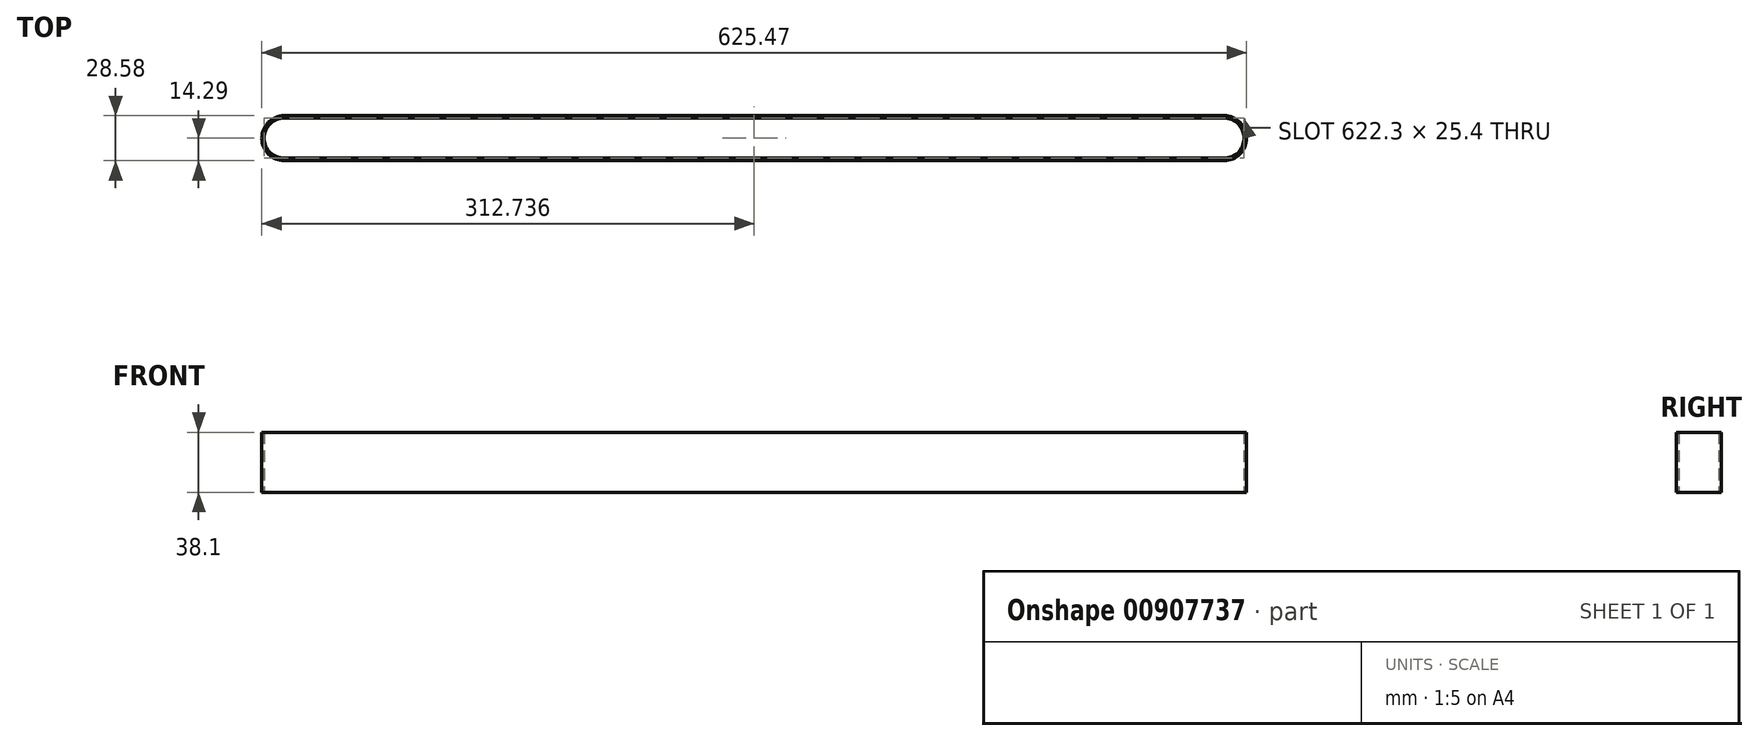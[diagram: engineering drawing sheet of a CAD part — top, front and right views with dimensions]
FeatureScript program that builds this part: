
annotation { "Feature Type Name" : "Feature", "Feature Type Description" : "" }
export const myFeature = defineFeature(function(context is Context, id is Id, definition is map)
    precondition{}
    {
        {
            var Q0;
            Q0=qCreatedBy(makeId("Top.planeOp"),FACE);
            var sketch = newSketch(context, id + "F0", { "sketchPlane" : qUnion([Q0])});
            skArc(sketch, "E0", {"start": v(-70.61, 14.29) * mm, "mid": v(-84.9, 0) * mm, "end": v(-70.61, -14.29) * mm});
            skArc(sketch, "E1", {"start": v(526.29, -14.29) * mm, "mid": v(540.57, 0) * mm, "end": v(526.29, 14.29) * mm});
            skLineSegment(sketch, "E2", {"start": v(-70.61, 14.29) * mm, "end": v(526.29, 14.29) * mm});
            skLineSegment(sketch, "E3", {"start": v(526.29, -14.29) * mm, "end": v(-70.61, -14.29) * mm});
            skArc(sketch, "E4", {"start": v(-70.61, 12.7) * mm, "mid": v(-83.31, 0) * mm, "end": v(-70.61, -12.7) * mm});
            skArc(sketch, "E5", {"start": v(526.29, -12.7) * mm, "mid": v(538.99, 0) * mm, "end": v(526.29, 12.7) * mm});
            skLineSegment(sketch, "E6", {"start": v(-70.61, 12.7) * mm, "end": v(526.29, 12.7) * mm});
            skLineSegment(sketch, "E7", {"start": v(526.29, -12.7) * mm, "end": v(-70.61, -12.7) * mm});
            skSolve(sketch);
        }
        {
            var Q0;
            Q0 = qSketchRegion(id + "F0", true);
            extrude(context, id + "F1", {"entities" : qUnion([Q0]), "depth" : 38.1 * mm, "offsetDistance" : 25.4 * mm});
        }
    });
